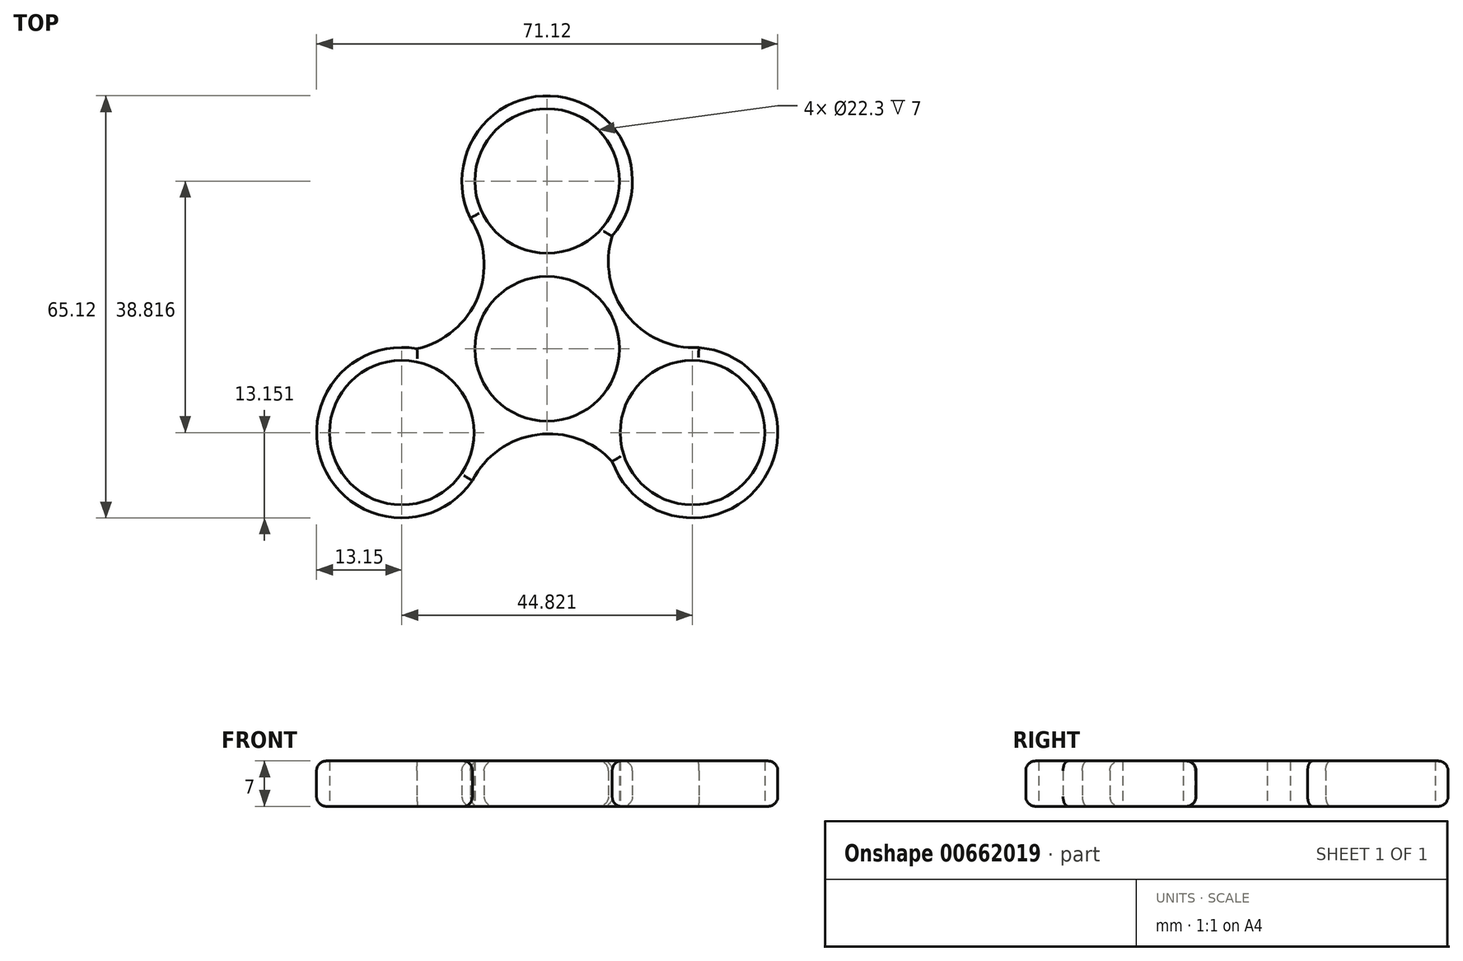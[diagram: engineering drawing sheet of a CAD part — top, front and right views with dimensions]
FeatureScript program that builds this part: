
annotation { "Feature Type Name" : "Feature", "Feature Type Description" : "" }
export const myFeature = defineFeature(function(context is Context, id is Id, definition is map)
    precondition{}
    {
        {
            var Q0;
            Q0=qCreatedBy(makeId("Top.planeOp"),FACE);
            var sketch = newSketch(context, id + "F0", { "sketchPlane" : qUnion([Q0])});
            skCircle(sketch, "E0", {"center": v(0, 0) * mm, "radius": 11.15 * mm});
            skArc(sketch, "E1", {"start": v(-11.14, 6.98) * mm, "mid": v(-11.46, 6.45) * mm, "end": v(-11.75, 5.9) * mm});
            skCircle(sketch, "E2", {"center": v(0, 25.88) * mm, "radius": 11.15 * mm});
            skArc(sketch, "E3.1.0", {"start": v(-20.06, 0) * mm, "mid": v(-34.2, -18.76) * mm, "end": v(-10.71, -18.94) * mm});
            skCircle(sketch, "E3.1.1", {"center": v(-22.41, -12.94) * mm, "radius": 11.15 * mm});
            skCircle(sketch, "E3.2.1", {"center": v(22.41, -12.94) * mm, "radius": 11.15 * mm});
            skArc(sketch, "E4", {"start": v(-20.06, 0) * mm, "mid": v(-10.7, 7.94) * mm, "end": v(-11.84, 20.16) * mm});
            skArc(sketch, "E5.1.0", {"start": v(10.03, -17.37) * mm, "mid": v(-1.52, -13.24) * mm, "end": v(-11.54, -20.34) * mm});
            skArc(sketch, "E5.2.0", {"start": v(10.03, 17.37) * mm, "mid": v(12.23, 5.3) * mm, "end": v(23.38, 0.18) * mm});
            skArc(sketch, "E6.trimOffspring", {"start": v(11.62, 6.16) * mm, "mid": v(11.32, 6.7) * mm, "end": v(11, 7.22) * mm});
            skArc(sketch, "E7.trimOffspring", {"start": v(-0.47, -13.14) * mm, "mid": v(0.14, -13.15) * mm, "end": v(0.76, -13.13) * mm});
            skArc(sketch, "E8.trimOffspring", {"start": v(10.03, 17.37) * mm, "mid": v(0.85, 39) * mm, "end": v(-11.05, 18.75) * mm});
            skArc(sketch, "E9.trimOffspring", {"start": v(10.03, -17.37) * mm, "mid": v(33.35, -20.24) * mm, "end": v(21.76, 0.2) * mm});
            skSolve(sketch);
        }
        {
            var Q0;
            Q0=makeQuery(id+"F0.imprint","IMPRINT",FACE,{"disambiguationData":[TD([[makeQuery(id+"F0.imprint","IMPRINT",EDGE,{"derivedFrom":sQuery(id+"F0.wireOp",EDGE,"E0")}),-1.0]])]});
            extrude(context, id + "F1", {"entities" : qUnion([Q0]), "depth" : 7 * mm, "offsetDistance" : 25 * mm});
        }
        {
            var Q0;
            Q0=makeQuery(id+"F1.opExtrude","CAP_EDGE",EDGE,{"disambiguationData":[OSD([sQuery(id+"F0.wireOp",EDGE,"E3.1.0")])],"isStart":false});
            var Q1;
            Q1=makeQuery(id+"F1.opExtrude","CAP_EDGE",EDGE,{"disambiguationData":[OSD([sQuery(id+"F0.wireOp",EDGE,"E4")])],"isStart":false});
            var Q2;
            Q2=makeQuery(id+"F1.opExtrude","CAP_EDGE",EDGE,{"disambiguationData":[OSD([sQuery(id+"F0.wireOp",EDGE,"E8.trimOffspring")])],"isStart":false});
            var Q3;
            Q3=makeQuery(id+"F1.opExtrude","CAP_EDGE",EDGE,{"disambiguationData":[OSD([sQuery(id+"F0.wireOp",EDGE,"E5.2.0")])],"isStart":false});
            var Q4;
            Q4=makeQuery(id+"F1.opExtrude","CAP_EDGE",EDGE,{"disambiguationData":[OSD([sQuery(id+"F0.wireOp",EDGE,"E9.trimOffspring")])],"isStart":false});
            var Q5;
            Q5=makeQuery(id+"F1.opExtrude","CAP_EDGE",EDGE,{"disambiguationData":[OSD([sQuery(id+"F0.wireOp",EDGE,"E5.1.0")])],"isStart":false});
            var Q6;
            Q6=makeQuery(id+"F1.opExtrude","CAP_EDGE",EDGE,{"disambiguationData":[OSD([sQuery(id+"F0.wireOp",EDGE,"E8.trimOffspring")])],"isStart":true});
            var Q7;
            Q7=makeQuery(id+"F1.opExtrude","CAP_EDGE",EDGE,{"disambiguationData":[OSD([sQuery(id+"F0.wireOp",EDGE,"E5.2.0")])],"isStart":true});
            var Q8;
            Q8=makeQuery(id+"F1.opExtrude","CAP_EDGE",EDGE,{"disambiguationData":[OSD([sQuery(id+"F0.wireOp",EDGE,"E9.trimOffspring")])],"isStart":true});
            var Q9;
            Q9=makeQuery(id+"F1.opExtrude","CAP_EDGE",EDGE,{"disambiguationData":[OSD([sQuery(id+"F0.wireOp",EDGE,"E5.1.0")])],"isStart":true});
            var Q10;
            Q10=makeQuery(id+"F1.opExtrude","CAP_EDGE",EDGE,{"disambiguationData":[OSD([sQuery(id+"F0.wireOp",EDGE,"E3.1.0")])],"isStart":true});
            var Q11;
            Q11=makeQuery(id+"F1.opExtrude","CAP_EDGE",EDGE,{"disambiguationData":[OSD([sQuery(id+"F0.wireOp",EDGE,"E4")])],"isStart":true});
            fillet(context, id + "F2", {"entities" : qUnion([Q0, Q1, Q2, Q3, Q4, Q5, Q6, Q7, Q8, Q9, Q10, Q11]), "radius" : 1.5 * mm, "tangentPropagation" : true, "allowEdgeOverflow" : false});
        }
    });
